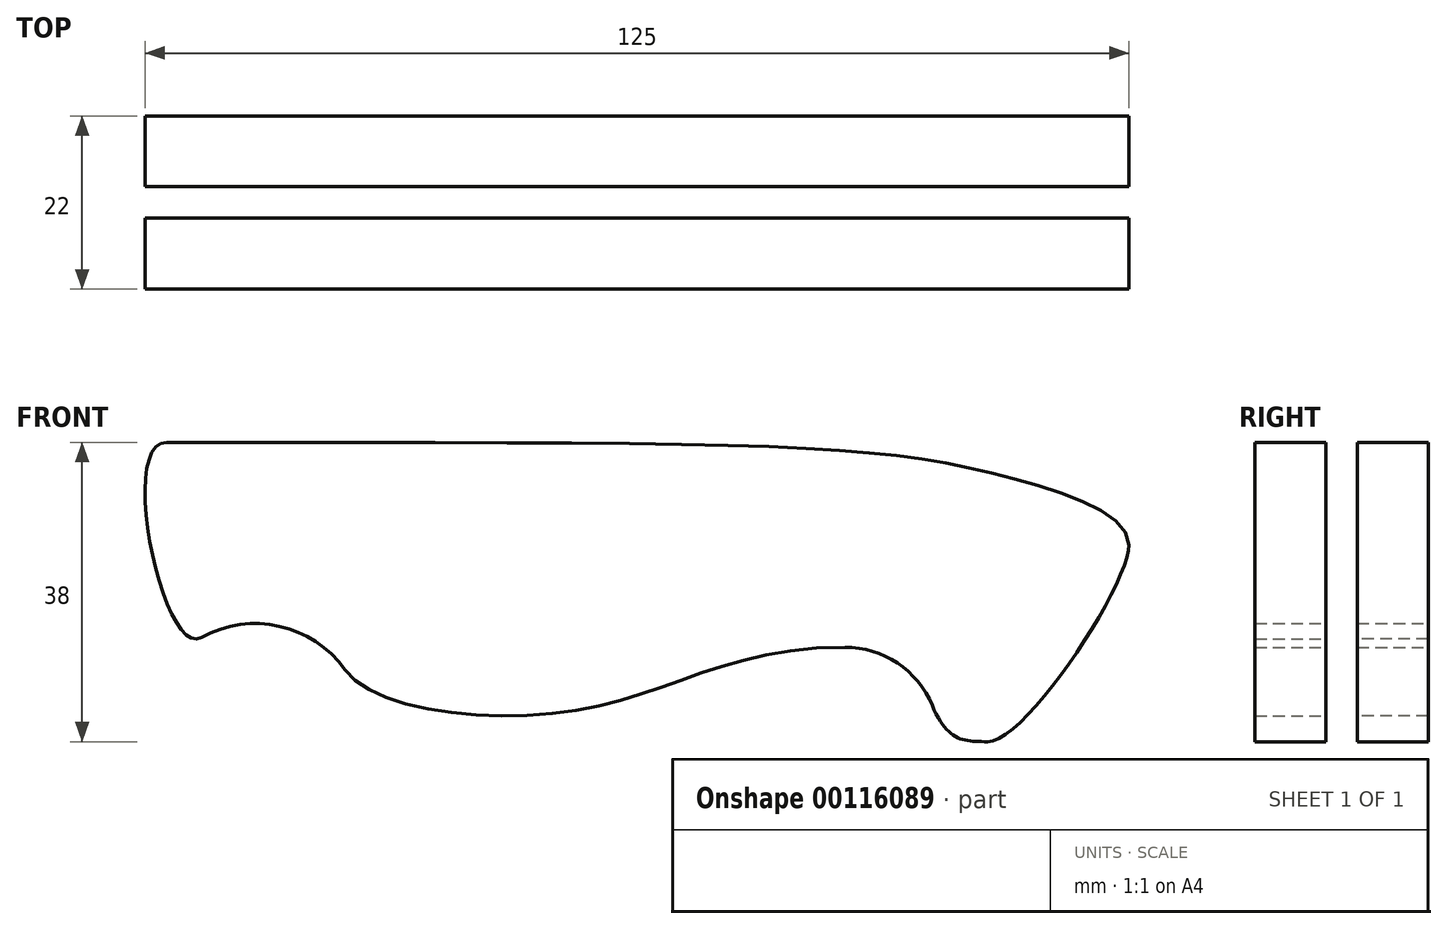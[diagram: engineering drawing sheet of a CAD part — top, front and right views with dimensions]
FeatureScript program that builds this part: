
annotation { "Feature Type Name" : "Feature", "Feature Type Description" : "" }
export const myFeature = defineFeature(function(context is Context, id is Id, definition is map)
    precondition{}
    {
        {
            var Q0;
            Q0=qCreatedBy(makeId("Front.planeOp"),FACE);
            var sketch = newSketch(context, id + "F0", { "sketchPlane" : qUnion([Q0])});
            skLineSegment(sketch, "E0", {"start": v(0, 38) * mm, "end": v(-240, 38) * mm});
            skLineSegment(sketch, "E1", {"start": v(-240, 38) * mm, "end": v(-240, 0) * mm});
            skLineSegment(sketch, "E2", {"start": v(-240, 0) * mm, "end": v(0, 0) * mm});
            skLineSegment(sketch, "E3", {"start": v(0, 0) * mm, "end": v(0, 38) * mm});
            skSolve(sketch);
        }
        {
            var Q0;
            Q0=makeQuery(id+"F0.imprint","IMPRINT",FACE,{"disambiguationData":[TD([[makeQuery(id+"F0.imprint","IMPRINT",EDGE,{"derivedFrom":sQuery(id+"F0.wireOp",EDGE,"E0")}),1.0]])]});
            var sketch = newSketch(context, id + "F1", { "sketchPlane" : qUnion([Q0])});
            skLineSegment(sketch, "E4", {"start": v(0, 50) * mm, "end": v(-125, 50) * mm, "construction": true});
            skLineSegment(sketch, "E5", {"start": v(-125, 50) * mm, "end": v(-240, 50) * mm, "construction": true});
            skLineSegment(sketch, "E6", {"start": v(-125, 50) * mm, "end": v(-125, 0) * mm, "construction": true});
            skLineSegment(sketch, "E7", {"start": v(-240, 0) * mm, "end": v(-240, 30) * mm, "construction": true});
            skLineSegment(sketch, "E8", {"start": v(0, 0) * mm, "end": v(0, 25) * mm, "construction": true});
            skFitSpline(sketch, "E9", {"points": [v(-240, 30) * mm, v(-125, 38) * mm], "startDerivative": vector(108.51, 24) * mm, "endDerivative": vector(182.2, 0) * mm});
            skLineSegment(sketch, "E10", {"start": v(0, 0) * mm, "end": v(-18, 0) * mm, "construction": true});
            skFitSpline(sketch, "E11", {"points": [v(-240, 30) * mm, v(-125, 0) * mm], "startDerivative": vector(22.07, -90) * mm, "endDerivative": vector(212.78, 0) * mm});
            skLineSegment(sketch, "E12", {"start": v(-111, 0) * mm, "end": v(-111, 1) * mm, "construction": true});
            skLineSegment(sketch, "E13", {"start": v(-111, 1) * mm, "end": v(-125, 1) * mm, "construction": true});
            skArc(sketch, "E14", {"start": v(-99.6, 9.13) * mm, "mid": v(-115.27, 14.33) * mm, "end": v(-125, 1) * mm});
            skLineSegment(sketch, "E15", {"start": v(-125, 38) * mm, "end": v(-15, 38) * mm, "construction": true});
            skFitSpline(sketch, "E16", {"points": [v(-125, 38) * mm, v(-15, 33.5) * mm, v(0, 25) * mm], "startDerivative": vector(334.98, 0) * mm, "endDerivative": vector(0, -42.32) * mm});
            skFitSpline(sketch, "E17", {"points": [v(0, 25) * mm, v(-18, 0) * mm], "startDerivative": vector(0, -15) * mm, "endDerivative": vector(-15, 0) * mm});
            skLineSegment(sketch, "E18", {"start": v(-125, 38) * mm, "end": v(-45, 38) * mm, "construction": true});
            skLineSegment(sketch, "E19", {"start": v(0, 29) * mm, "end": v(0, 25) * mm, "construction": true});
            skLineSegment(sketch, "E20", {"start": v(0, 25) * mm, "end": v(0, 20) * mm, "construction": true});
            skLineSegment(sketch, "E21", {"start": v(-18, 0) * mm, "end": v(-13, 0) * mm, "construction": true});
            skLineSegment(sketch, "E22", {"start": v(-125, -8.92) * mm, "end": v(-25, -8.92) * mm, "construction": true});
            skLineSegment(sketch, "E23", {"start": v(-36.08, 0) * mm, "end": v(-36.08, 12) * mm, "construction": true});
            skArc(sketch, "E24", {"start": v(-25, 4.62) * mm, "mid": v(-29.42, 9.98) * mm, "end": v(-36.08, 12) * mm});
            skPoint(sketch, "E25", {"position": v(-99.6, 9.13) * mm});
            skFitSpline(sketch, "E26", {"points": [v(-99.6, 9.13) * mm, v(-70, 4) * mm, v(-36.08, 12) * mm], "startDerivative": vector(23.51, -32.98) * mm, "endDerivative": vector(86.78, 0) * mm});
            skPoint(sketch, "E27", {"position": v(-25, 4.62) * mm});
            skLineSegment(sketch, "E28", {"start": v(-25, 4.62) * mm, "end": v(-23.08, 0) * mm, "construction": true});
            skFitSpline(sketch, "E29", {"points": [v(-18, 0) * mm, v(-25, 4.62) * mm], "startDerivative": vector(-9, 0) * mm, "endDerivative": vector(-5.77, 13.85) * mm});
            skLineSegment(sketch, "E30", {"start": v(-125, 0) * mm, "end": v(-125, 1) * mm});
            skLineSegment(sketch, "E31", {"start": v(-25, -8.92) * mm, "end": v(-25, 4.62) * mm, "construction": true});
            skLineSegment(sketch, "E32", {"start": v(-15, 33.5) * mm, "end": v(-15, 38) * mm, "construction": true});
            skLineSegment(sketch, "E33", {"start": v(-18, 0) * mm, "end": v(-21, 0) * mm, "construction": true});
            skLineSegment(sketch, "E34", {"start": v(-125, -5.42) * mm, "end": v(-70, -5.42) * mm, "construction": true});
            skLineSegment(sketch, "E35", {"start": v(-125, -8.92) * mm, "end": v(-129, -8.92) * mm, "construction": true});
            skLineSegment(sketch, "E36", {"start": v(-129, 0) * mm, "end": v(-129, 38) * mm});
            skLineSegment(sketch, "E37", {"start": v(-111, 1) * mm, "end": v(-99.6, 1) * mm, "construction": true});
            skLineSegment(sketch, "E38", {"start": v(-99.6, 1) * mm, "end": v(-99.6, 9.13) * mm, "construction": true});
            skLineSegment(sketch, "E39", {"start": v(-70, 4) * mm, "end": v(-70, 0) * mm, "construction": true});
            skLineSegment(sketch, "E40", {"start": v(-99.6, 9.13) * mm, "end": v(-95.83, 3.83) * mm, "construction": true});
            skLineSegment(sketch, "E41", {"start": v(-36.08, 12) * mm, "end": v(-51.08, 12) * mm, "construction": true});
            skFitSpline(sketch, "E42", {"points": [v(-122.25, 38) * mm, v(-117.83, 13.22) * mm], "startDerivative": vector(-18.9, 0) * mm, "endDerivative": vector(14.63, 8.17) * mm});
            skLineSegment(sketch, "E43", {"start": v(-117.83, 13.22) * mm, "end": v(-122.7, 10.5) * mm});
            skSolve(sketch);
        }
        {
            var Q0;
            Q0=makeQuery(id+"F1.imprint","IMPRINT",FACE,{"disambiguationData":[TD([[makeQuery(id+"F1.imprint","IMPRINT",EDGE,{"derivedFrom":sQuery(id+"F1.wireOp",EDGE,"E9")}),-1.0]])]});
            extrude(context, id + "F2", {"entities" : qUnion([Q0]), "endBound" : BoundingType.SYMMETRIC, "depth" : 4 * mm});
        }
        {
            var Q0;
            Q0=makeQuery(id+"F2.opExtrude","CAP_EDGE",EDGE,{"disambiguationData":[OSD([sQuery(id+"F1.wireOp",EDGE,"E11")])],"isStart":false});
            var Q1;
            Q1=makeQuery(id+"F2.opExtrude","CAP_EDGE",EDGE,{"disambiguationData":[OSD([sQuery(id+"F1.wireOp",EDGE,"E11")])],"isStart":true});
            chamfer(context, id + "F3", {"entities" : qUnion([Q0, Q1]), "chamferType" : ChamferType.TWO_OFFSETS, "width1" : 20 * mm, "oppositeDirection" : false, "width2" : 2 * mm});
        }
        {
            var Q0;
            Q0=makeQuery(id+"F1.imprint","IMPRINT",FACE,{"disambiguationData":[TD([[makeQuery(id+"F1.imprint","IMPRINT",EDGE,{"derivedFrom":sQuery(id+"F1.wireOp",EDGE,"E14")}),-1.0]])]});
            var Q1;
            {var subQ0=sQuery(id+"F1.wireOp",EDGE,"E17");Q1=makeQuery(id+"F1.imprint","IMPRINT",FACE,{"disambiguationData":[TD([[makeQuery(id+"F1.imprint","IMPRINT",EDGE,{"derivedFrom":subQ0}),-1.0]])]});}
            extrude(context, id + "F4", {"entities" : qUnion([Q0, Q1]), "operationType" : NewBodyOperationType.ADD, "endBound" : BoundingType.SYMMETRIC, "depth" : 4 * mm});
        }
        {
            var Q0;
            {var subQ0=sQuery(id+"F1.wireOp",EDGE,"E17");Q0=makeQuery(id+"F1.imprint","IMPRINT",FACE,{"disambiguationData":[TD([[makeQuery(id+"F1.imprint","IMPRINT",EDGE,{"derivedFrom":subQ0}),-1.0]])]});}
            extrude(context, id + "F5", {"entities" : qUnion([Q0]), "endBound" : BoundingType.SYMMETRIC, "depth" : 22 * mm});
        }
        {
            var Q0;
            Q0 = qSketchRegion(id + "F0", true);
            extrude(context, id + "F6", {"entities" : qUnion([Q0]), "operationType" : NewBodyOperationType.REMOVE, "endBound" : BoundingType.SYMMETRIC, "oppositeDirection" : true, "depth" : 4 * mm});
        }
    });
